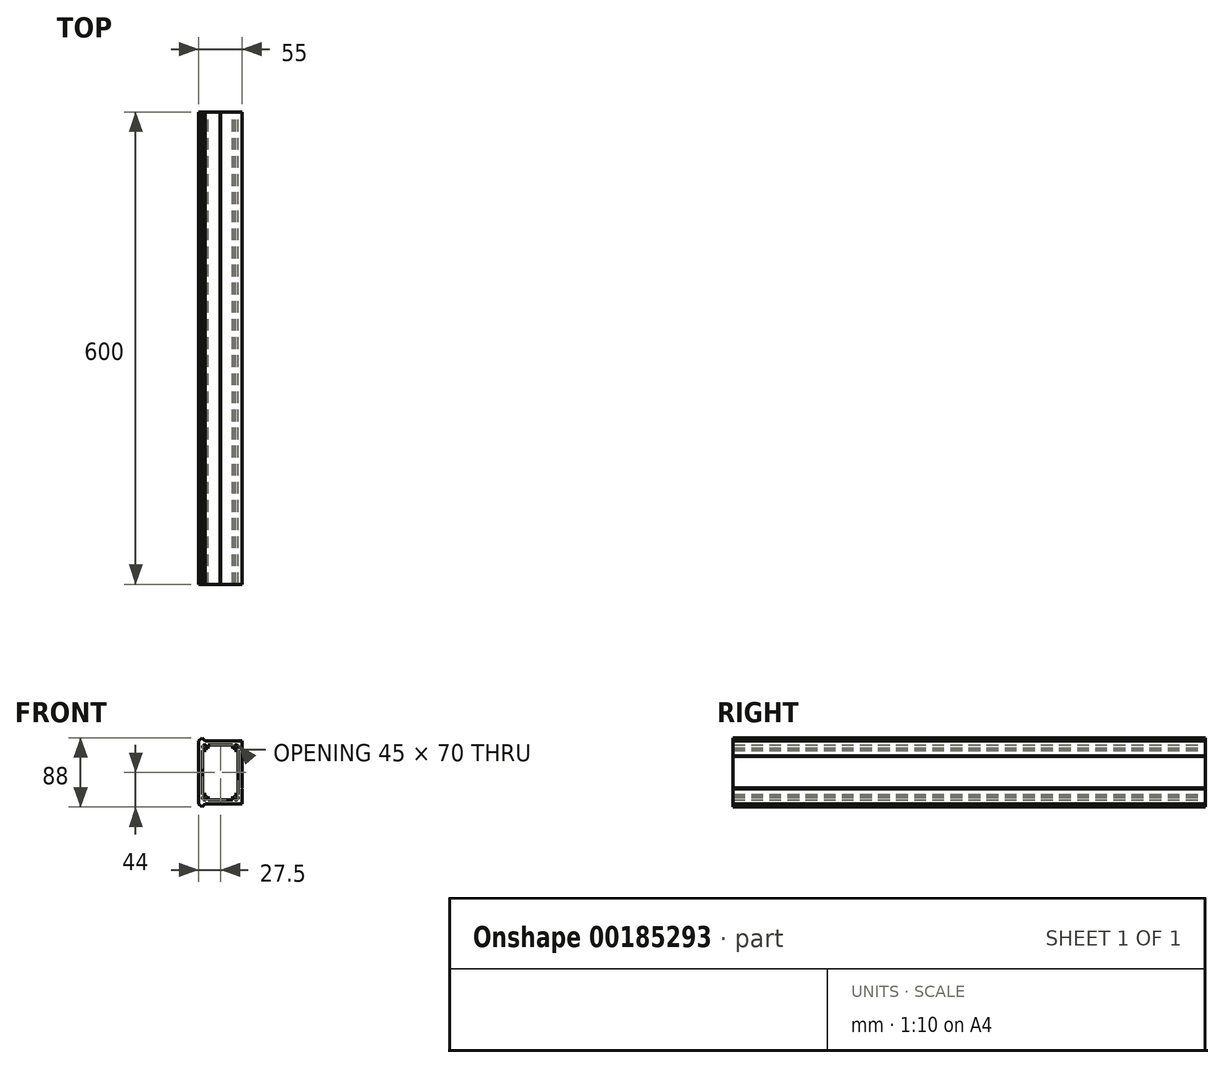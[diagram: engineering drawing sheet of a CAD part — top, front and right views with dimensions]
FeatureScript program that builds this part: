
annotation { "Feature Type Name" : "Feature", "Feature Type Description" : "" }
export const myFeature = defineFeature(function(context is Context, id is Id, definition is map)
    precondition{}
    {
        {
            var Q0;
            Q0=qCreatedBy(makeId("Front.planeOp"),FACE);
            var sketch = newSketch(context, id + "F0", { "sketchPlane" : qUnion([Q0])});
            skLineSegment(sketch, "E0", {"start": v(0, 0) * mm, "end": v(0, 80) * mm});
            skLineSegment(sketch, "E1", {"start": v(0, 80) * mm, "end": v(4, 84) * mm});
            skLineSegment(sketch, "E2", {"start": v(4, 84) * mm, "end": v(8, 80) * mm});
            skLineSegment(sketch, "E3", {"start": v(8, 80) * mm, "end": v(27, 80) * mm});
            skLineSegment(sketch, "E4", {"start": v(27, 80) * mm, "end": v(27.5, 79.5) * mm});
            skLineSegment(sketch, "E5", {"start": v(27.5, 79.5) * mm, "end": v(28, 80) * mm});
            skLineSegment(sketch, "E6", {"start": v(28, 80) * mm, "end": v(55, 80) * mm});
            skLineSegment(sketch, "E7", {"start": v(55, 80) * mm, "end": v(55, 61) * mm});
            skLineSegment(sketch, "E8", {"start": v(55, 61) * mm, "end": v(54.5, 60.5) * mm});
            skLineSegment(sketch, "E9", {"start": v(54.5, 60.5) * mm, "end": v(55, 60) * mm});
            skLineSegment(sketch, "E10", {"start": v(55, 60) * mm, "end": v(55, 20) * mm});
            skLineSegment(sketch, "E11", {"start": v(55, 20) * mm, "end": v(54.5, 19.5) * mm});
            skLineSegment(sketch, "E12", {"start": v(54.5, 19.5) * mm, "end": v(55, 19) * mm});
            skLineSegment(sketch, "E13", {"start": v(55, 19) * mm, "end": v(55, 0) * mm});
            skLineSegment(sketch, "E14", {"start": v(55, 0) * mm, "end": v(28, 0) * mm});
            skLineSegment(sketch, "E15", {"start": v(28, 0) * mm, "end": v(27.5, 0.5) * mm});
            skLineSegment(sketch, "E16", {"start": v(27.5, 0.5) * mm, "end": v(27, 0) * mm});
            skLineSegment(sketch, "E17", {"start": v(27, 0) * mm, "end": v(8, 0) * mm});
            skLineSegment(sketch, "E18", {"start": v(8, 0) * mm, "end": v(4, -4) * mm});
            skLineSegment(sketch, "E19", {"start": v(4, -4) * mm, "end": v(0, 0) * mm});
            skSolve(sketch);
        }
        {
            var Q0;
            Q0=makeQuery(id+"F0.imprint","IMPRINT",FACE,{"disambiguationData":[TD([[makeQuery(id+"F0.imprint","IMPRINT",EDGE,{"derivedFrom":sQuery(id+"F0.wireOp",EDGE,"E0")}),-1.0]])]});
            extrude(context, id + "F1", {"entities" : qUnion([Q0]), "depth" : 600 * mm});
        }
        {
            var Q0;
            Q0=qCreatedBy(makeId("Front.planeOp"),FACE);
            var sketch = newSketch(context, id + "F2", { "sketchPlane" : qUnion([Q0])});
            skLineSegment(sketch, "E20.bottom", {"start": v(7.5, 72.5) * mm, "end": v(47.5, 72.5) * mm, "construction": true});
            skLineSegment(sketch, "E20.top", {"start": v(7.5, 7.5) * mm, "end": v(47.5, 7.5) * mm, "construction": true});
            skLineSegment(sketch, "E20.left", {"start": v(7.5, 72.5) * mm, "end": v(7.5, 7.5) * mm, "construction": true});
            skLineSegment(sketch, "E20.right", {"start": v(47.5, 72.5) * mm, "end": v(47.5, 7.5) * mm, "construction": true});
            skLineSegment(sketch, "E21.bottom", {"start": v(5, 75) * mm, "end": v(50, 75) * mm, "construction": true});
            skLineSegment(sketch, "E21.top", {"start": v(5, 5) * mm, "end": v(50, 5) * mm, "construction": true});
            skLineSegment(sketch, "E21.left", {"start": v(5, 75) * mm, "end": v(5, 5) * mm, "construction": true});
            skLineSegment(sketch, "E21.right", {"start": v(50, 75) * mm, "end": v(50, 5) * mm, "construction": true});
            skLineSegment(sketch, "E22.bottom", {"start": v(9.4, 70.6) * mm, "end": v(45.6, 70.6) * mm, "construction": true});
            skLineSegment(sketch, "E22.top", {"start": v(9.4, 9.4) * mm, "end": v(45.6, 9.4) * mm, "construction": true});
            skLineSegment(sketch, "E22.left", {"start": v(9.4, 70.6) * mm, "end": v(9.4, 9.4) * mm, "construction": true});
            skLineSegment(sketch, "E22.right", {"start": v(45.6, 70.6) * mm, "end": v(45.6, 9.4) * mm, "construction": true});
            skLineSegment(sketch, "E23", {"start": v(9.4, 12) * mm, "end": v(5, 12) * mm});
            skLineSegment(sketch, "E24", {"start": v(5, 12) * mm, "end": v(5, 68) * mm});
            skLineSegment(sketch, "E25", {"start": v(5, 68) * mm, "end": v(9.4, 68) * mm});
            skLineSegment(sketch, "E26", {"start": v(9.4, 68) * mm, "end": v(12, 70.6) * mm, "construction": true});
            skLineSegment(sketch, "E27", {"start": v(12, 70.6) * mm, "end": v(12, 75) * mm});
            skLineSegment(sketch, "E28", {"start": v(12, 75) * mm, "end": v(43, 75) * mm});
            skLineSegment(sketch, "E29", {"start": v(43, 75) * mm, "end": v(43, 70.6) * mm});
            skLineSegment(sketch, "E30", {"start": v(43, 70.6) * mm, "end": v(45.6, 68) * mm, "construction": true});
            skLineSegment(sketch, "E31", {"start": v(45.6, 68) * mm, "end": v(50, 68) * mm});
            skLineSegment(sketch, "E32", {"start": v(50, 68) * mm, "end": v(50, 12) * mm});
            skLineSegment(sketch, "E33", {"start": v(50, 12) * mm, "end": v(45.6, 12) * mm});
            skLineSegment(sketch, "E34", {"start": v(45.6, 12) * mm, "end": v(43, 9.4) * mm, "construction": true});
            skLineSegment(sketch, "E35", {"start": v(43, 9.4) * mm, "end": v(43, 5) * mm});
            skLineSegment(sketch, "E36", {"start": v(43, 5) * mm, "end": v(12, 5) * mm});
            skLineSegment(sketch, "E37", {"start": v(12, 5) * mm, "end": v(12, 9.4) * mm});
            skLineSegment(sketch, "E38", {"start": v(12, 9.4) * mm, "end": v(9.4, 12) * mm, "construction": true});
            skArc(sketch, "E39", {"start": v(9.65, 71.23) * mm, "mid": v(5.73, 74.27) * mm, "end": v(8.77, 70.35) * mm});
            skLineSegment(sketch, "E40", {"start": v(8.77, 70.35) * mm, "end": v(9.4, 68) * mm});
            skLineSegment(sketch, "E41", {"start": v(9.65, 71.23) * mm, "end": v(12, 70.6) * mm});
            skLineSegment(sketch, "E42", {"start": v(7.5, 72.5) * mm, "end": v(9.4, 70.6) * mm, "construction": true});
            skLineSegment(sketch, "E43", {"start": v(9.65, 71.23) * mm, "end": v(8.77, 70.35) * mm, "construction": true});
            skPoint(sketch, "E44", {"position": v(9.21, 70.79) * mm});
            skArc(sketch, "E45", {"start": v(8.16, 9.91) * mm, "mid": v(5.73, 5.73) * mm, "end": v(9.91, 8.16) * mm});
            skLineSegment(sketch, "E46", {"start": v(9.4, 12) * mm, "end": v(8.16, 9.91) * mm});
            skLineSegment(sketch, "E47", {"start": v(12, 9.4) * mm, "end": v(9.91, 8.16) * mm});
            skArc(sketch, "E48", {"start": v(45.09, 8.16) * mm, "mid": v(49.27, 5.73) * mm, "end": v(46.84, 9.91) * mm});
            skLineSegment(sketch, "E49", {"start": v(43, 9.4) * mm, "end": v(45.09, 8.16) * mm});
            skLineSegment(sketch, "E50", {"start": v(45.6, 12) * mm, "end": v(46.84, 9.91) * mm});
            skArc(sketch, "E51", {"start": v(45.35, 71.23) * mm, "mid": v(49.27, 74.27) * mm, "end": v(46.23, 70.35) * mm});
            skLineSegment(sketch, "E52", {"start": v(45.35, 71.23) * mm, "end": v(46.23, 70.35) * mm, "construction": true});
            skLineSegment(sketch, "E53", {"start": v(47.5, 72.5) * mm, "end": v(44.3, 69.3) * mm, "construction": true});
            skPoint(sketch, "E54", {"position": v(45.79, 70.79) * mm});
            skLineSegment(sketch, "E55", {"start": v(45.35, 71.23) * mm, "end": v(43, 70.6) * mm});
            skLineSegment(sketch, "E56", {"start": v(46.23, 70.35) * mm, "end": v(45.6, 68) * mm});
            skSolve(sketch);
        }
        {
            var Q0;
            Q0=qSketchRegion(id+"F2",true);
            extrude(context, id + "F3", {"entities" : qUnion([Q0]), "operationType" : NewBodyOperationType.REMOVE, "endBound" : BoundingType.UP_TO_NEXT, "depth" : 600 * mm});
        }
    });
